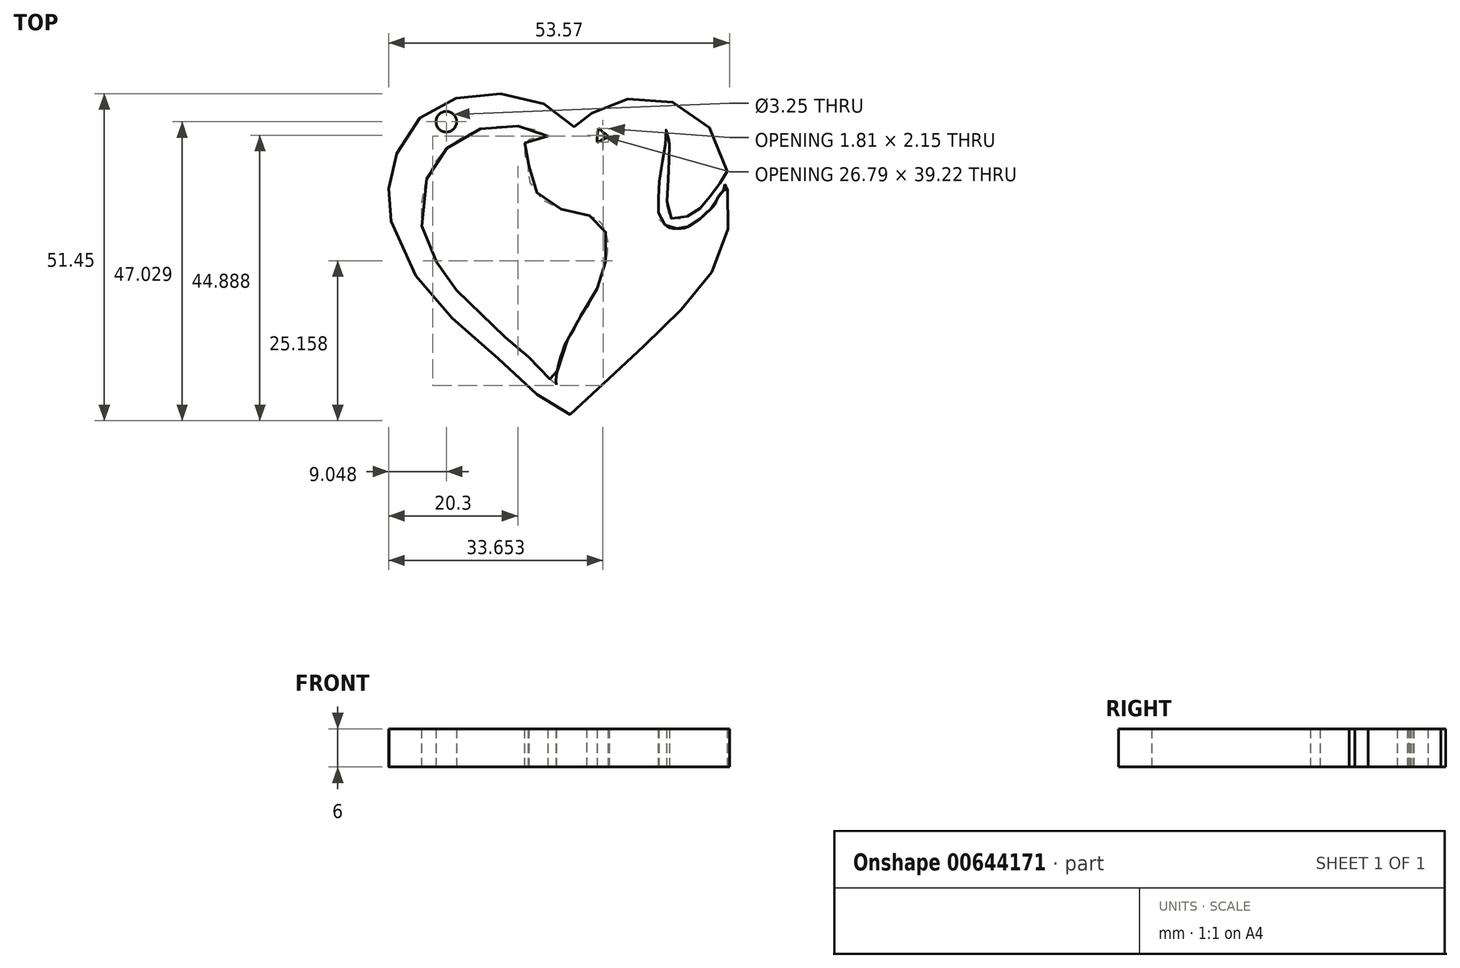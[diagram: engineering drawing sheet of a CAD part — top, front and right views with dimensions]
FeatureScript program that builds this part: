
annotation { "Feature Type Name" : "Feature", "Feature Type Description" : "" }
export const myFeature = defineFeature(function(context is Context, id is Id, definition is map)
    precondition{}
    {
        {
            var Q0;
            Q0=qCreatedBy(makeId("Top.planeOp"),FACE);
            var sketch = newSketch(context, id + "F0", { "sketchPlane" : qUnion([Q0])});
            skFitSpline(sketch, "E0", {"points": [v(9, 14.93) * mm, v(9.49, 15.15) * mm, v(10.38, 15.53) * mm, v(10.46, 15.68) * mm, v(10.46, 16.1) * mm, v(10.53, 16.61) * mm, v(10.97, 17.27) * mm, v(11.45, 18) * mm, v(12.13, 18.47) * mm, v(13.05, 18.95) * mm, v(14.01, 19.35) * mm, v(15.21, 19.71) * mm, v(16.21, 19.87) * mm, v(17.81, 19.91) * mm, v(19.57, 19.95) * mm, v(21.01, 19.83) * mm, v(22.25, 19.71) * mm, v(22.77, 19.55) * mm, v(24.21, 19.35) * mm, v(25.45, 18.91) * mm, v(26.3, 18.55) * mm, v(27.65, 17.63) * mm, v(29.05, 16.47) * mm, v(29.73, 15.31) * mm, v(30.45, 14.03) * mm, v(31.01, 12.55) * mm, v(31.73, 10.95) * mm, v(32.3, 9.23) * mm, v(32.52, 8.54) * mm, v(32.63, 7.04) * mm, v(32.54, 5.57) * mm, v(32.71, 4.63) * mm, v(32.8, 4.07) * mm, v(32.77, 2.93) * mm, v(32.83, 2.25) * mm, v(32.81, 0.8) * mm, v(32.62, -0.44) * mm, v(32.29, -1.44) * mm, v(32, -3.1) * mm, v(31.24, -4.82) * mm, v(30.62, -6.15) * mm, v(30.15, -7.15) * mm, v(29.53, -8.15) * mm, v(28.3, -9.72) * mm, v(27.48, -10.72) * mm, v(26.63, -11.86) * mm, v(25.4, -13.14) * mm, v(23.58, -14.9) * mm, v(22.16, -16.33) * mm, v(20.82, -17.8) * mm, v(19.92, -18.47) * mm, v(19.16, -19.23) * mm, v(17.83, -20.42) * mm, v(16.6, -21.66) * mm, v(15.4, -22.8) * mm, v(14.45, -23.6) * mm, v(13.45, -24.51) * mm, v(12.36, -25.47) * mm, v(10.86, -26.97) * mm, v(9.18, -28.35) * mm, v(7.8, -29.73) * mm, v(6.96, -30.68) * mm, v(6.48, -30.56) * mm, v(5.88, -29.73) * mm, v(4.39, -28.23) * mm, v(3, -27.03) * mm, v(1.5, -25.47) * mm, v(0.61, -24.7) * mm, v(-0.83, -23.43) * mm, v(-1.85, -22.41) * mm, v(-4, -20.56) * mm, v(-5.92, -19.18) * mm, v(-7.6, -17.68) * mm, v(-9.88, -15.34) * mm, v(-11.14, -14.2) * mm, v(-12.33, -13) * mm, v(-13.41, -11.87) * mm, v(-14.55, -10.43) * mm, v(-16.59, -7.73) * mm, v(-18.33, -4.97) * mm, v(-18.99, -3.48) * mm, v(-19.7, -1.62) * mm, v(-20.37, 0.78) * mm, v(-20.5, 1.52) * mm, v(-20.69, 2.28) * mm, v(-20.6, 2.79) * mm, v(-20.66, 3.6) * mm, v(-20.66, 4.25) * mm, v(-20.69, 5.06) * mm, v(-20.72, 5.84) * mm, v(-20.69, 6.83) * mm, v(-20.48, 8) * mm, v(-20.36, 8.9) * mm, v(-20.15, 9.53) * mm, v(-19.82, 10.34) * mm, v(-19.6, 11.03) * mm, v(-19.25, 11.83) * mm, v(-18.7, 12.97) * mm, v(-18.1, 14.17) * mm, v(-17.25, 15.15) * mm, v(-16.45, 16.17) * mm, v(-15.72, 16.96) * mm, v(-14.42, 18) * mm, v(-13.72, 18.42) * mm, v(-13.18, 18.7) * mm, v(-12.1, 19.28) * mm, v(-11.18, 19.7) * mm, v(-9.72, 20.1) * mm, v(-8.55, 20.36) * mm, v(-7.25, 20.61) * mm, v(-5.91, 20.7) * mm, v(-4.68, 20.74) * mm, v(-3.06, 20.7) * mm, v(-1.75, 20.58) * mm, v(-0.33, 20.4) * mm, v(1, 20.07) * mm, v(2.5, 19.56) * mm, v(3.48, 19.25) * mm, v(4.75, 18.58) * mm, v(5.52, 18.2) * mm, v(6.5, 17.44) * mm, v(7.3, 16.77) * mm, v(7.76, 16.24) * mm, v(8.23, 15.74) * mm, v(8.67, 15.2) * mm, v(9, 14.93) * mm]});
            skFitSpline(sketch, "E1", {"points": [v(4.32, 14.06) * mm, v(3.24, 13.94) * mm, v(2.36, 13.86) * mm, v(1.44, 13.54) * mm, v(0.8, 13.18) * mm, v(0.64, 12.62) * mm, v(0.6, 11.58) * mm, v(0.76, 10.74) * mm, v(1.12, 9.86) * mm, v(1.28, 9.58) * mm, v(1.16, 8.74) * mm, v(1.32, 7.62) * mm, v(1.72, 6.22) * mm, v(2.52, 5.22) * mm, v(3.28, 4.26) * mm, v(4.36, 3.5) * mm, v(5.44, 3.02) * mm, v(6.72, 2.46) * mm, v(7.88, 2.22) * mm, v(8.76, 1.94) * mm, v(10.16, 1.7) * mm, v(11.28, 1.42) * mm, v(11.92, 1.06) * mm, v(12.4, 0.7) * mm, v(12.92, 0) * mm, v(13.32, -0.9) * mm, v(13.6, -1.94) * mm, v(13.72, -3.22) * mm, v(13.56, -4.38) * mm, v(13.36, -5.9) * mm, v(13, -7.02) * mm, v(12.56, -8.22) * mm, v(12.36, -9.06) * mm, v(11.84, -10.3) * mm, v(11.03, -11.52) * mm, v(10.56, -12.67) * mm, v(10.02, -13.34) * mm, v(9.34, -14.48) * mm, v(8.74, -15.5) * mm, v(8.2, -16.7) * mm, v(7.6, -17.64) * mm, v(7, -18.79) * mm, v(6.52, -20.13) * mm, v(5.98, -21.82) * mm, v(5.71, -23.3) * mm, v(5.58, -24.37) * mm, v(5.58, -25.47) * mm, v(5.1, -24.9) * mm, v(4.37, -23.9) * mm, v(3.43, -23.1) * mm, v(2.42, -21.88) * mm, v(1.5, -20.94) * mm, v(0.53, -20) * mm, v(-0.75, -19.26) * mm, v(-1.49, -18.18) * mm, v(-2.7, -17.38) * mm, v(-3.7, -16.37) * mm, v(-4.85, -15.22) * mm, v(-6.06, -14.08) * mm, v(-7.34, -12.94) * mm, v(-8.55, -11.86) * mm, v(-9.83, -10.58) * mm, v(-10.57, -9.44) * mm, v(-11.71, -7.96) * mm, v(-12.65, -6.55) * mm, v(-13.6, -5.2) * mm, v(-14.27, -3.11) * mm, v(-15.34, -0.76) * mm, v(-15.61, 1.46) * mm, v(-15.28, 5.7) * mm, v(-14.47, 7.85) * mm, v(-13.46, 9.8) * mm, v(-12.25, 11.42) * mm, v(-11.1, 12.56) * mm, v(-9.15, 13.9) * mm, v(-7.54, 14.71) * mm, v(-5.32, 15.52) * mm, v(-3.97, 15.59) * mm, v(-1.55, 15.72) * mm, v(0.73, 15.45) * mm, v(2.15, 15.12) * mm, v(3.63, 14.44) * mm, v(4.32, 14.06) * mm]});
            skFitSpline(sketch, "E2", {"points": [v(12.3, 15.25) * mm, v(12.1, 14.17) * mm, v(12.1, 13.1) * mm, v(13.18, 13.64) * mm, v(13.92, 13.9) * mm, v(13.11, 14.51) * mm, v(12.3, 15.25) * mm]});
            skFitSpline(sketch, "E3", {"points": [v(32.52, 7.76) * mm, v(32.63, 7.04) * mm, v(32.54, 5.57) * mm, v(32.15, 6.45) * mm, v(31.94, 5.57) * mm, v(31.43, 5) * mm, v(30.83, 3.95) * mm, v(30.45, 3.14) * mm, v(29.7, 2.42) * mm, v(28.8, 1.57) * mm, v(27.83, 0.68) * mm, v(26.64, 0) * mm, v(25.83, -0.42) * mm, v(24.82, -0.5) * mm, v(23.67, -0.46) * mm, v(22.83, 0) * mm, v(21.8, 0.9) * mm, v(21.72, 2.5) * mm, v(21.68, 3.82) * mm, v(21.68, 5.57) * mm, v(21.94, 7.76) * mm, v(22.4, 10.74) * mm, v(22.7, 12.34) * mm, v(22.83, 14.06) * mm, v(22.9, 15.05) * mm, v(23.38, 13.6) * mm, v(23.38, 11.91) * mm, v(23.33, 9.96) * mm, v(23.25, 7.46) * mm, v(23.08, 4.24) * mm, v(23.2, 1.49) * mm, v(24.69, 0.98) * mm, v(26.34, 1.49) * mm, v(27.74, 2.3) * mm, v(28.8, 3.35) * mm, v(29.82, 4.63) * mm, v(31, 6.2) * mm, v(31.85, 7.42) * mm, v(32.52, 8.54) * mm, v(32.52, 7.76) * mm]});
            skCircle(sketch, "E4", {"center": v(-11.67, 16.32) * mm, "radius": 1.62 * mm});
            skSolve(sketch);
        }
        {
            var Q0;
            Q0=makeQuery(id+"F0.imprint","IMPRINT",FACE,{"disambiguationData":[TD([[makeQuery(id+"F0.imprint","IMPRINT",EDGE,{"derivedFrom":sQuery(id+"F0.wireOp",EDGE,"E1")}),1.0]])]});
            extrude(context, id + "F1", {"entities" : qUnion([Q0]), "depth" : 6 * mm, "offsetDistance" : 25 * mm});
        }
    });
